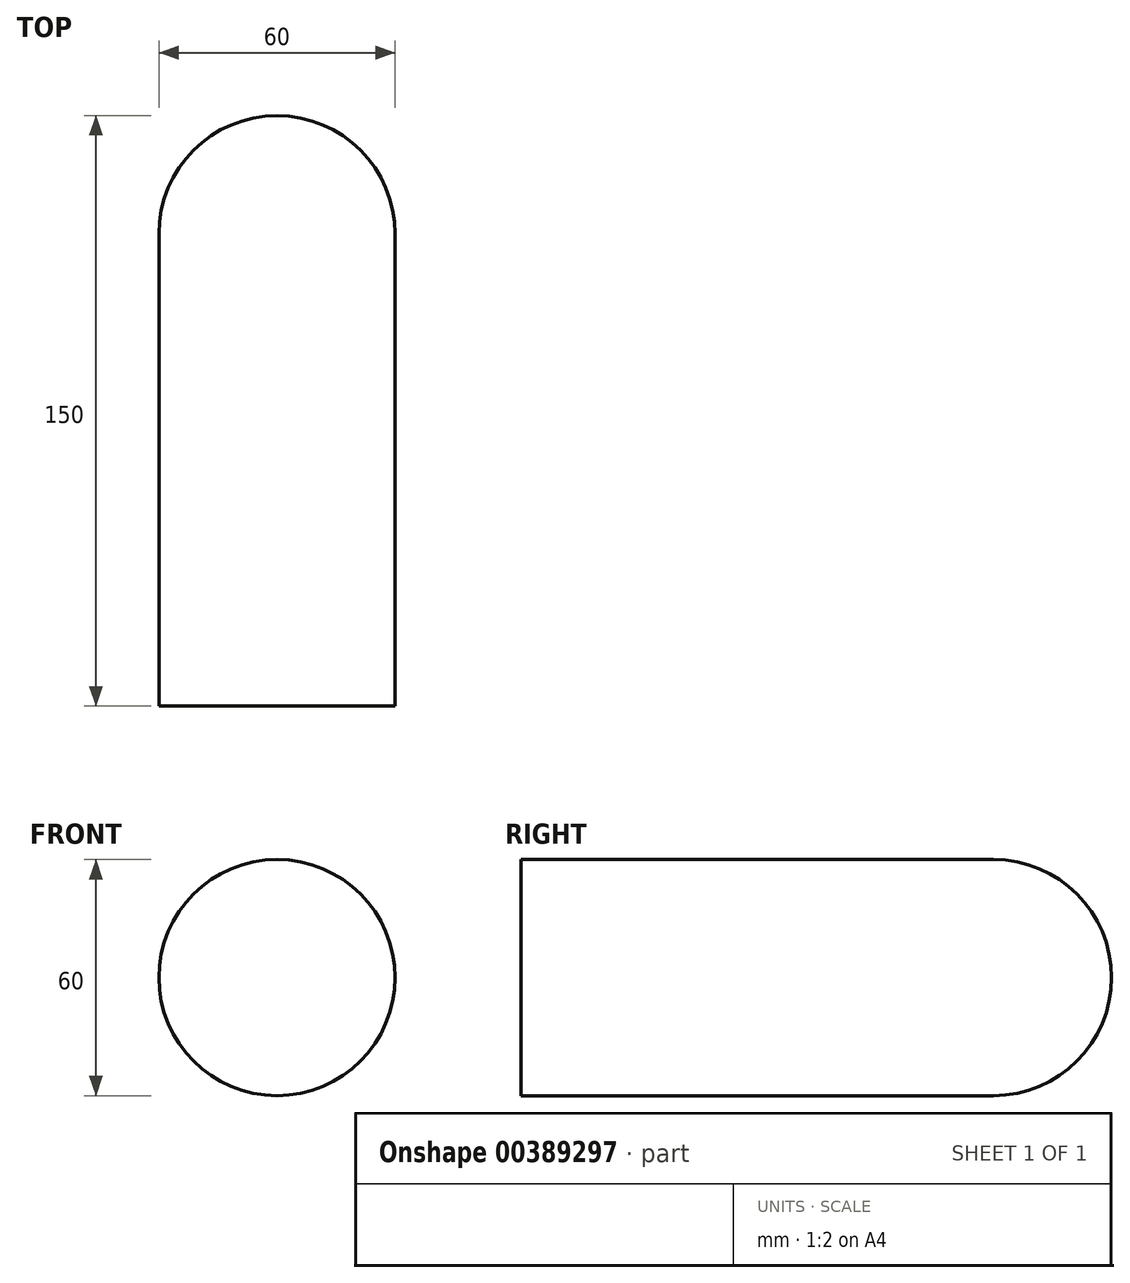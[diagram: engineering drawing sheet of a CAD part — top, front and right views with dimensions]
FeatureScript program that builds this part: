
annotation { "Feature Type Name" : "Feature", "Feature Type Description" : "" }
export const myFeature = defineFeature(function(context is Context, id is Id, definition is map)
    precondition{}
    {
        {
            var Q0;
            Q0=qCreatedBy(makeId("Top.planeOp"),FACE);
            var sketch = newSketch(context, id + "F0", { "sketchPlane" : qUnion([Q0])});
            skLineSegment(sketch, "E0", {"start": v(-40.23, 5.22) * mm, "end": v(-40.23, -114.78) * mm});
            skPoint(sketch, "E1.end.orphan", {"position": v(0, -26.73) * mm});
            skLineSegment(sketch, "E2", {"start": v(-10.23, 35.22) * mm, "end": v(-10.23, 35.22) * mm});
            skLineSegment(sketch, "E3", {"start": v(19.77, 5.22) * mm, "end": v(19.77, -114.78) * mm});
            skLineSegment(sketch, "E4", {"start": v(19.77, -114.78) * mm, "end": v(-40.23, -114.78) * mm});
            skPoint(sketch, "E5.visualSharp", {"position": v(-40.23, 35.22) * mm});
            skArc(sketch, "E5.filletArc", {"start": v(-10.23, 35.22) * mm, "mid": v(-31.45, 26.44) * mm, "end": v(-40.23, 5.22) * mm});
            skPoint(sketch, "E6.visualSharp", {"position": v(19.77, 35.22) * mm});
            skArc(sketch, "E6.filletArc", {"start": v(19.77, 5.22) * mm, "mid": v(10.98, 26.44) * mm, "end": v(-10.23, 35.22) * mm});
            skSolve(sketch);
        }
        {
            var Q0;
            Q0=makeQuery(id+"F0.imprint","IMPRINT",FACE,{"disambiguationData":[TD([[makeQuery(id+"F0.imprint","IMPRINT",EDGE,{"derivedFrom":sQuery(id+"F0.wireOp",EDGE,"E0")}),1.0]])]});
            extrude(context, id + "F1", {"entities" : qUnion([Q0]), "depth" : 60 * mm});
        }
        {
            var Q0;
            Q0=makeQuery(id+"F1.opExtrude","CAP_EDGE",EDGE,{"disambiguationData":[OSD([sQuery(id+"F0.wireOp",EDGE,"E0")])],"isStart":true});
            var Q1;
            Q1=makeQuery(id+"F1.opExtrude","CAP_EDGE",EDGE,{"disambiguationData":[OSD([sQuery(id+"F0.wireOp",EDGE,"E0")])],"isStart":false});
            fillet(context, id + "F2", {"entities" : qUnion([Q0, Q1]), "radius" : 30 * mm, "tangentPropagation" : true, "allowEdgeOverflow" : false});
        }
    });
